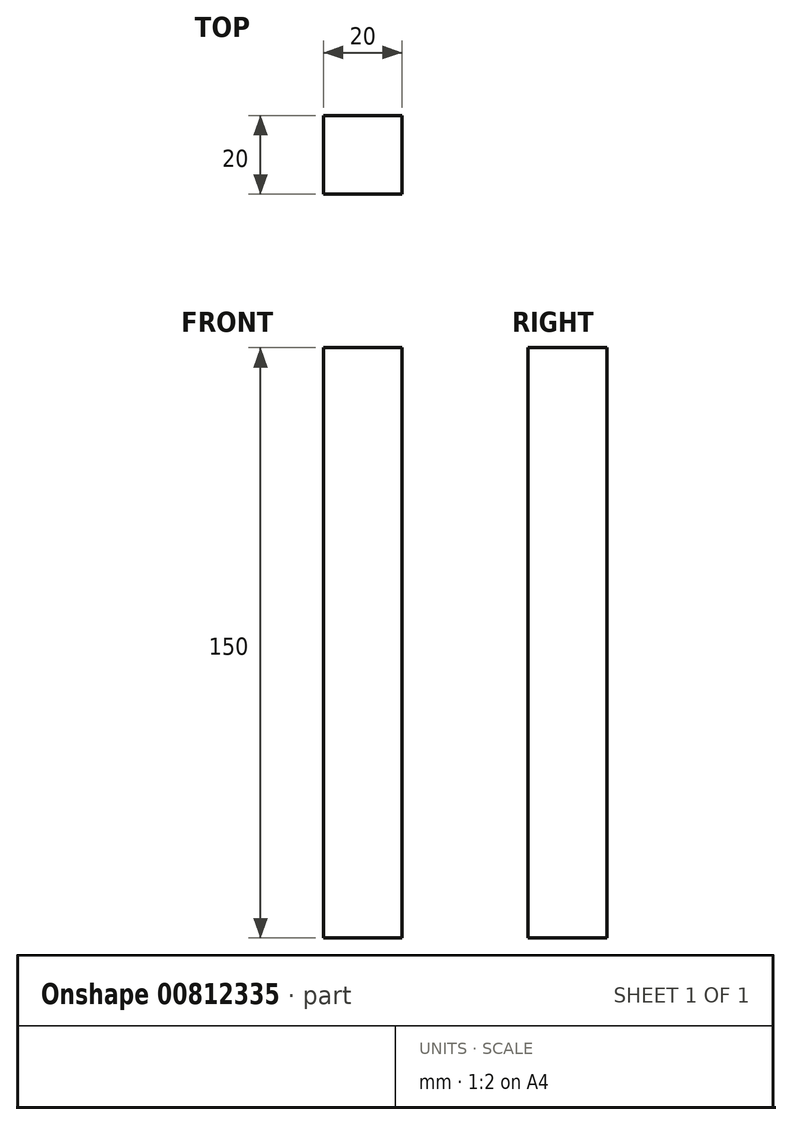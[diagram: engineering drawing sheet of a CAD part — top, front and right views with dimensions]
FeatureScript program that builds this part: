
annotation { "Feature Type Name" : "Feature", "Feature Type Description" : "" }
export const myFeature = defineFeature(function(context is Context, id is Id, definition is map)
    precondition{}
    {
        {
            var Q0;
            Q0=qCreatedBy(makeId("Top.planeOp"),FACE);
            var sketch = newSketch(context, id + "F0", { "sketchPlane" : qUnion([Q0])});
            skLineSegment(sketch, "E0.bottom", {"start": v(-10, 10) * mm, "end": v(10, 10) * mm});
            skLineSegment(sketch, "E0.top", {"start": v(-10, -10) * mm, "end": v(10, -10) * mm});
            skLineSegment(sketch, "E0.left", {"start": v(-10, 10) * mm, "end": v(-10, -10) * mm});
            skLineSegment(sketch, "E0.right", {"start": v(10, 10) * mm, "end": v(10, -10) * mm});
            skSolve(sketch);
        }
        {
            var Q0;
            Q0=makeQuery(id+"F0.imprint","IMPRINT",FACE,{"disambiguationData":[TD([[makeQuery(id+"F0.imprint","IMPRINT",EDGE,{"derivedFrom":sQuery(id+"F0.wireOp",EDGE,"E0.bottom")}),-1.0]])]});
            extrude(context, id + "F1", {"entities" : qUnion([Q0]), "depth" : 150 * mm, "offsetDistance" : 25 * mm});
        }
    });
